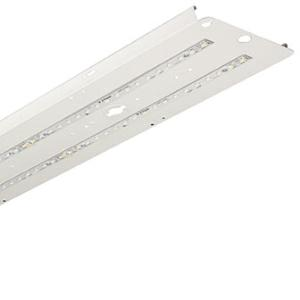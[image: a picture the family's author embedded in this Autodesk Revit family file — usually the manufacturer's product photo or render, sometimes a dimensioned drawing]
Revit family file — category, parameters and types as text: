
# Revit family: 3f_filippi_-_kit_led_retrofit_per_schermo_in_vetro_3f_filippi_-_a5148_-_kit_led_i3f_76_a3f_91_a3f_93-l1265-2x18w_1e58
name_source: partatom
category: Lighting Fixtures
units: mm (PartAtom-declared; Revit-internal decimal feet)

## family parameters
Cut with Voids When Loaded = No
Host = Face
Light Source = No
Part Type = Normal
Room Calculation Point = No
Round Connector Dimension = Use Diameter
Shared = No

## types (1)
- 3F Filippi - Kit LED Retrofit per schermo in vetro (1 x LED, 5383 lm, 40 W, 4000 K)
    Apparent Load = 40 VA
    Approval mark = ENEC
    CIE Flux Codes = 52 87 99 100 100
    Color Rendering = 80
    Color Temperature = 4000 K
    Control Gear = Electronic ballast
    Default Elevation = 1800 mm
    Description = Led retrofit kit suitable for Fluorescent Beta 2x i3F 76, A3F 91 and A3F 93 luminaires.

ILLUMINOTECHNICAL
Luminous efficiency 100% (DLOR 100%, ULOR 0%).
Initial luminous flux of the luminaire 5383 lm.
Symmetric distribution.
Installation Interdistance Transv.D = 1.29 x hu - Long.D = 1.29 x hu.
Tabular UGR (CIE 117 - 4H-8H; S=0.25H; 70/50/20): RUG 20 - 22.7.
Beam angle: 106° - 113°.
Luminous efficacy 135 lm/W.
Lifetime (L93/B10): 30000 h. (tq+25°C)
Lifetime (L90/B10): 50000 h. (tq+25°C)
Lifetime (L85/B10): 80000 h. (tq+25°C)
Lifetime (L80/B10): 100000 h. (tq+25°C)
Lifetime (L85/B10): 50000 h. (tq+35°C)
Sudden decreased luminous flux after 50000 hours: 0% (C0).
Photobiological safety in compliance with IEC/TR 62778: RG0 risk exempt, (IEC 62471).
In compliance with IEC/EN 62722-2-1 - IEC/EN 62717 standards.

SOURCE
2 linear LED modules 18W/840.
Energy efficiency class (UE 2019/2020 - UE 2019/2015): D.
CIE 13.3 Colour rendering index: CRI >80 (R9 <50%).
IES TM-30 Fidelity Index: Rf = 84 Rg = 95.
CCT nominal colour temperature 4000 K.
Colour initial tolerance (MacAdam): SDCM 3.

MECHANICAL
Gear-tray unit in hot-galvanised steel, painted in white polyester, fixed to the housing by means of "Ribloc" rapid devices in galvanised steel, hinged opening.
Luminaire with limited surface temperature. - D - (EN 60598-2-24)
Dimensions: 1265x235 mm, height 105 mm. Weight 1.4 kg.
Glow-wire test resistance 850°C.

ELECTRICAL
Halogen Free electronic wiring 230V-50/60Hz, power factor 0.95, THD <25%, constant output current, SELV, class I, 1 driver.
Power of the luminaire 40 W.
CE - IEC 60598-1 - EN 60598-1.
SAFE FLICKER: PstLM=<1 and SVM=<0.4 (IEC TR 61547-1 and IEC TR 63158), to ensure a more comfortable and safe light.
Luminaire compliant with EN 60598-2-22 for power supply from a centralised emergency system CPSS (Central Power Supply System), not incorporated in the luminaire - high risk areas excluded. The default power and flux are 100% in AC and 100% in DC.
Ambient temperature from -20°C to +35°C.
Temperature class T6 max 85°C.
Relative humidity UR: <85%.

INSTALLATION
Retrofit.
Correct installation of the retrofit LED kit, compliant with EN 60598-1 and CE marked, inside the 3F Filippi - Beta 2x i3F 76, A3F 91 and A3F 93 Fluorescent luminaires must be only carried out by qualified personnel to ensure compliance with the national installation standards.
Attention: to maintain the degree of protection of the device and for the purposes of validity of the guarantee of the new retrofit kits, it is imperative to replace the old cable guides (on the body of the device) with the new ones supplied.
All accessories dedicated to this product are available on the Catalog and on our website www.3F-Filippi.com.

WARNING
Fixture not suitable for cold stores with an ambient temperature <0°C and/or relative humidity >85%.
Luminaire designed for disposal/recycling at end-of-life.
Replaceable (LED only) light source by a professional. Replaceable control gear by a professional.
    Height = 105 mm
    Lamp = 1 x LED
    Lamp Light Flux = 5383 lm
    Lamp Power = 40 W
    Lamp count = 1
    Length = 1265 mm
    Lifetime = 50000 h
    Luminous efficacy = 135 lm/W
    Manufacturer = 3F Filippi
    ModVariant = No
    Model = 3F Filippi - A5148 - KIT LED i3F 76,A3F 91,A3F 93-L1265-2x18W
    Mounting Place = Ceiling
    Mounting Type = Surface mounted
    Number of Poles = 1
    OnlyDefault = Yes
    Power Factor = 1
    Product Name = 3F Filippi - Kit LED Retrofit per schermo in vetro
    Product group = ceiling mounted luminaire
    ProductGroupID = 3
    Protection Class = Protection class I
    Protection Degree = Degree of protection
    RLX_Detail_Level = 1
    RLX_Emergency_Light_Flux = 0 lm
    RLX_Emergency_Type = 0
    RLX_Emergency_Type_DB = No
    RlxData = <blob elided: 58181 chars, md5=07972d39>
    Socket = socket
    Standby Power = 0 W
    System Light Flux = 5383 lm
    System Power = 40 W
    Type Comments = Product without accessories
    Type Image = 3ffilippi_a5148.jpg
    URL = http://relux.com
    VarID = ---
    Voltage = 0 V
    Weight = 0.00 kg
    Width = 235 mm

## geometry (parser evidence)
native form markers: Blend x4, Sweep x10
no freeform markers — native parametric forms only
